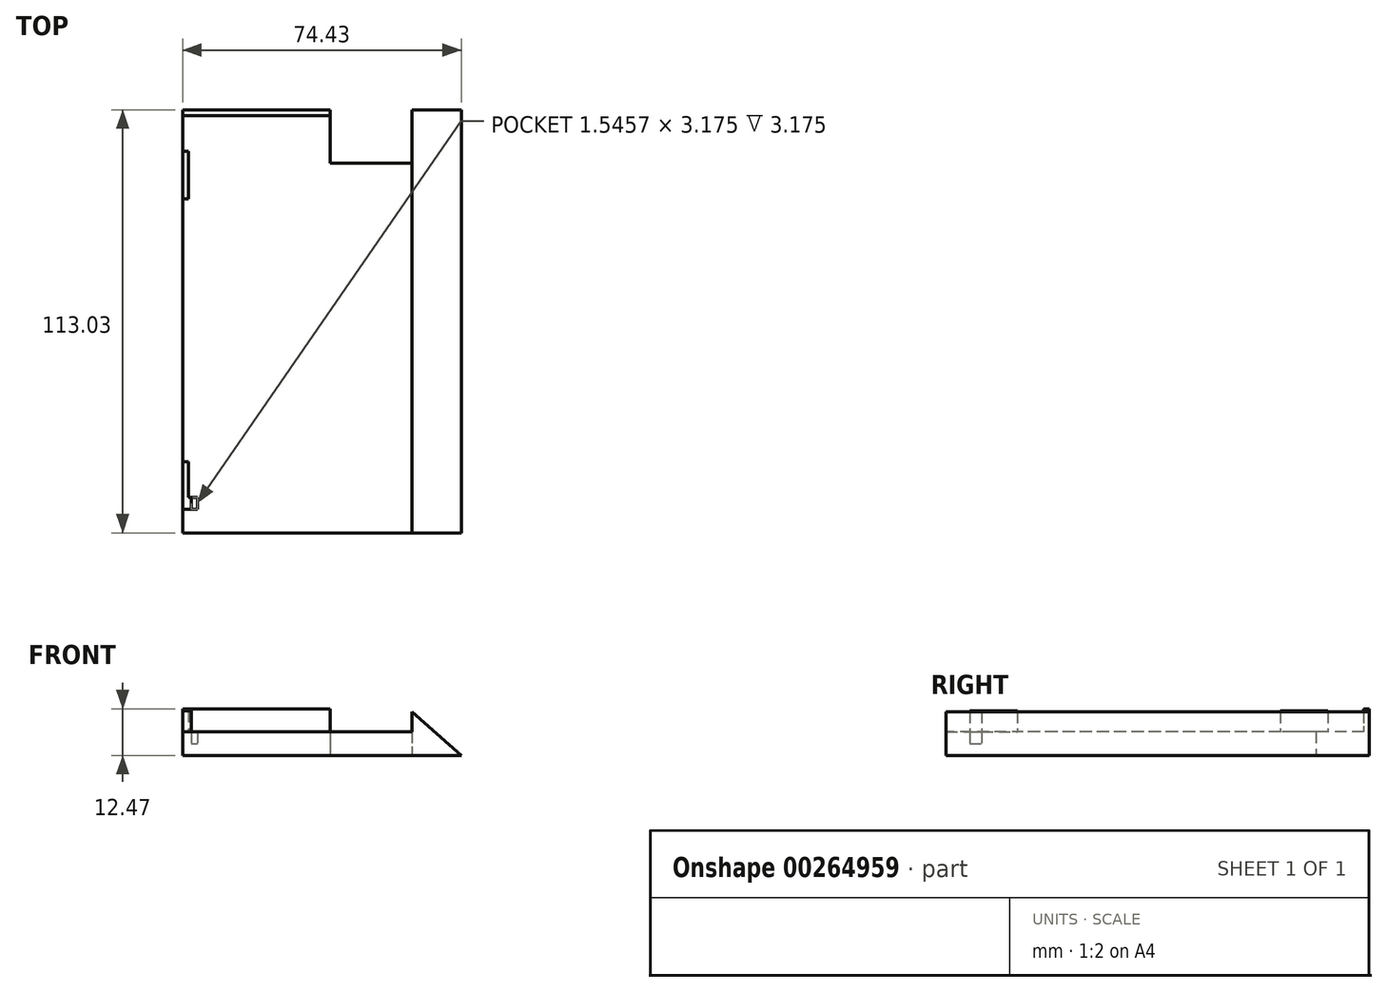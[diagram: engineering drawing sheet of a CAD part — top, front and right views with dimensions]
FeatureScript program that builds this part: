
annotation { "Feature Type Name" : "Feature", "Feature Type Description" : "" }
export const myFeature = defineFeature(function(context is Context, id is Id, definition is map)
    precondition{}
    {
        {
            var Q0;
            Q0=qCreatedBy(makeId("Top.planeOp"),FACE);
            var sketch = newSketch(context, id + "F0", { "sketchPlane" : qUnion([Q0])});
            skLineSegment(sketch, "E0.bottom", {"start": v(-36.5, 51.12) * mm, "end": v(2.98, 51.12) * mm});
            skLineSegment(sketch, "E0.top", {"start": v(-36.5, -61.91) * mm, "end": v(23.83, -61.91) * mm});
            skLineSegment(sketch, "E0.left", {"start": v(-36.5, 51.12) * mm, "end": v(-36.5, -6.67) * mm});
            skPoint(sketch, "E0.middle", {"position": v(0, -10.8) * mm});
            skLineSegment(sketch, "E1", {"start": v(-36.5, -61.91) * mm, "end": v(-34.91, -61.91) * mm});
            skLineSegment(sketch, "E2", {"start": v(-34.91, -61.91) * mm, "end": v(-34.91, -6.67) * mm});
            skLineSegment(sketch, "E3", {"start": v(-36.5, -61.91) * mm, "end": v(1.6, -61.91) * mm});
            skLineSegment(sketch, "E4", {"start": v(36.5, -61.91) * mm, "end": v(24.83, -61.91) * mm});
            skLineSegment(sketch, "E5", {"start": v(24.83, -52.15) * mm, "end": v(24.83, -61.91) * mm});
            skLineSegment(sketch, "E6", {"start": v(24.83, -52.15) * mm, "end": v(24.83, -6.67) * mm});
            skLineSegment(sketch, "E7", {"start": v(-36.5, 51.12) * mm, "end": v(-36.5, 49.53) * mm});
            skLineSegment(sketch, "E8", {"start": v(-36.5, 49.53) * mm, "end": v(2.98, 49.53) * mm});
            skLineSegment(sketch, "E9", {"start": v(2.98, 49.53) * mm, "end": v(2.98, 51.12) * mm});
            skLineSegment(sketch, "E10", {"start": v(2.98, 51.12) * mm, "end": v(2.98, 36.83) * mm});
            skLineSegment(sketch, "E11", {"start": v(2.98, 36.83) * mm, "end": v(24.03, 36.83) * mm});
            skLineSegment(sketch, "E12.trimOffspring", {"start": v(24.83, 51.12) * mm, "end": v(36.5, 51.12) * mm});
            skLineSegment(sketch, "E13", {"start": v(-36.5, -61.91) * mm, "end": v(-36.5, -55.56) * mm});
            skLineSegment(sketch, "E14", {"start": v(-36.5, -55.56) * mm, "end": v(-34.91, -55.56) * mm});
            skLineSegment(sketch, "E15", {"start": v(-36.5, -55.56) * mm, "end": v(-36.5, -52.39) * mm});
            skLineSegment(sketch, "E16", {"start": v(-36.5, -52.39) * mm, "end": v(-34.91, -52.39) * mm});
            skLineSegment(sketch, "E17", {"start": v(-34.91, -52.39) * mm, "end": v(-34.91, -55.56) * mm});
            skLineSegment(sketch, "E18", {"start": v(-36.5, -55.56) * mm, "end": v(-34.09, -55.56) * mm});
            skLineSegment(sketch, "E19", {"start": v(-34.09, -52.39) * mm, "end": v(-34.91, -52.39) * mm});
            skLineSegment(sketch, "E20", {"start": v(-36.5, 51.12) * mm, "end": v(-36.5, 40) * mm});
            skLineSegment(sketch, "E21", {"start": v(-36.5, 40) * mm, "end": v(-34.91, 40) * mm});
            skLineSegment(sketch, "E22", {"start": v(-34.91, 40) * mm, "end": v(-34.91, 36.83) * mm});
            skLineSegment(sketch, "E23", {"start": v(-34.94, 36.83) * mm, "end": v(-36.5, 36.83) * mm});
            skLineSegment(sketch, "E24", {"start": v(-36.5, 36.83) * mm, "end": v(-34.94, 36.83) * mm});
            skLineSegment(sketch, "E25", {"start": v(-33.97, 40) * mm, "end": v(-34.91, 40) * mm});
            skLineSegment(sketch, "E26.bottom", {"start": v(-36.5, -52.39) * mm, "end": v(-35.83, -52.39) * mm});
            skLineSegment(sketch, "E26.top", {"start": v(-35.83, -55.56) * mm, "end": v(-34.09, -55.56) * mm});
            skLineSegment(sketch, "E26.left", {"start": v(-35.83, -52.39) * mm, "end": v(-35.83, -55.56) * mm});
            skLineSegment(sketch, "E27.bottom", {"start": v(-35.72, 36.83) * mm, "end": v(-34.94, 36.83) * mm});
            skLineSegment(sketch, "E27.top", {"start": v(-35.72, 40) * mm, "end": v(-33.97, 40) * mm});
            skLineSegment(sketch, "E27.left", {"start": v(-35.72, 36.83) * mm, "end": v(-35.72, 40) * mm});
            skLineSegment(sketch, "E28.left", {"start": v(-35.83, -54.55) * mm, "end": v(-35.83, -53.37) * mm});
            skLineSegment(sketch, "E29.left", {"start": v(-35.72, 37.85) * mm, "end": v(-35.72, 38.9) * mm});
            skLineSegment(sketch, "E30", {"start": v(-34.09, -55.56) * mm, "end": v(-34.09, -52.39) * mm});
            skPoint(sketch, "E31.orphan", {"position": v(-32.54, -52.39) * mm});
            skPoint(sketch, "E32.start.orphan", {"position": v(-34.94, 36.83) * mm});
            skPoint(sketch, "E33.orphan", {"position": v(-32.54, 40) * mm});
            skPoint(sketch, "E34.orphan", {"position": v(23.83, 51.12) * mm});
            skLineSegment(sketch, "E35.trimOffspring", {"start": v(24.83, -61.91) * mm, "end": v(36.5, -61.91) * mm});
            skPoint(sketch, "E36.end.orphan", {"position": v(28.59, 51.12) * mm});
            skPoint(sketch, "E37.end.orphan", {"position": v(30.17, -61.91) * mm});
            skLineSegment(sketch, "E38", {"start": v(-34.09, -52.39) * mm, "end": v(-32.54, -52.39) * mm});
            skLineSegment(sketch, "E39", {"start": v(-32.54, -55.56) * mm, "end": v(-32.54, -52.39) * mm});
            skLineSegment(sketch, "E40", {"start": v(-32.54, -55.56) * mm, "end": v(-34.09, -55.56) * mm});
            skLineSegment(sketch, "E41", {"start": v(-34.91, 40) * mm, "end": v(-33.97, 40) * mm});
            skLineSegment(sketch, "E42", {"start": v(-34.91, 36.83) * mm, "end": v(-33.97, 36.83) * mm});
            skLineSegment(sketch, "E43", {"start": v(-34.91, 33.66) * mm, "end": v(-36.5, 33.66) * mm});
            skPoint(sketch, "E44.start.orphan", {"position": v(-32.54, 36.83) * mm});
            skLineSegment(sketch, "E45.MirrorCS", {"start": v(-36.5, -49.21) * mm, "end": v(-34.09, -49.21) * mm});
            skLineSegment(sketch, "E46.trimOffspring", {"start": v(-34.91, -52.39) * mm, "end": v(-34.09, -52.39) * mm});
            skLineSegment(sketch, "E47", {"start": v(24.03, 36.83) * mm, "end": v(24.83, 36.83) * mm});
            skLineSegment(sketch, "E48", {"start": v(24.57, 3.5) * mm, "end": v(24.83, 3.5) * mm});
            skLineSegment(sketch, "E49", {"start": v(24.57, -1.27) * mm, "end": v(24.83, -1.27) * mm});
            skLineSegment(sketch, "E50", {"start": v(24.57, -23.81) * mm, "end": v(24.83, -23.81) * mm});
            skLineSegment(sketch, "E51", {"start": v(24.57, -28.57) * mm, "end": v(24.83, -28.57) * mm});
            skLineSegment(sketch, "E52", {"start": v(23.83, -61.91) * mm, "end": v(24.83, -61.91) * mm});
            skPoint(sketch, "E53.end.orphan", {"position": v(39.05, 51.12) * mm});
            skLineSegment(sketch, "E54", {"start": v(-36.5, 33.66) * mm, "end": v(-36.5, 27.3) * mm});
            skLineSegment(sketch, "E55", {"start": v(-36.5, 27.3) * mm, "end": v(-34.91, 27.3) * mm});
            skLineSegment(sketch, "E56", {"start": v(-36.5, -49.21) * mm, "end": v(-36.5, -42.86) * mm});
            skLineSegment(sketch, "E57", {"start": v(-36.5, -42.86) * mm, "end": v(-34.91, -42.86) * mm});
            skLineSegment(sketch, "E58", {"start": v(36.5, -61.91) * mm, "end": v(37.93, -61.91) * mm});
            skLineSegment(sketch, "E59", {"start": v(37.93, -61.91) * mm, "end": v(37.93, -6.67) * mm});
            skLineSegment(sketch, "E60", {"start": v(37.93, 51.12) * mm, "end": v(36.5, 51.12) * mm});
            skLineSegment(sketch, "E61", {"start": v(36.5, -61.91) * mm, "end": v(36.5, -6.67) * mm});
            skLineSegment(sketch, "E62", {"start": v(36.5, 51.12) * mm, "end": v(36.5, -6.67) * mm});
            skLineSegment(sketch, "E63.trimOffspring", {"start": v(-36.5, -6.67) * mm, "end": v(-36.5, -61.91) * mm});
            skLineSegment(sketch, "E64.trimOffspring", {"start": v(-34.91, -6.67) * mm, "end": v(-34.91, 51.12) * mm});
            skLineSegment(sketch, "E65.trimOffspring", {"start": v(24.83, -6.67) * mm, "end": v(24.83, 51.12) * mm});
            skLineSegment(sketch, "E66.trimOffspring", {"start": v(36.5, -6.67) * mm, "end": v(36.5, -61.91) * mm});
            skLineSegment(sketch, "E67.trimOffspring", {"start": v(37.93, -6.67) * mm, "end": v(37.93, 51.12) * mm});
            skLineSegment(sketch, "E68.trimOffspring", {"start": v(36.5, -6.67) * mm, "end": v(36.5, 51.12) * mm});
            skSolve(sketch);
        }
        {
            var Q0;
            {var subQ12=sQuery(id+"F0.wireOp",EDGE,"E0.top");Q0=makeQuery(id+"F0.imprint","IMPRINT",FACE,{"disambiguationData":[TD([[makeQuery(id+"F0.imprint","IMPRINT",EDGE,{"derivedFrom":subQ12}),1.0]])]});}
            var Q1;
            {var subQ0=sQuery(id+"F0.wireOp",EDGE,"E17");Q1=makeQuery(id+"F0.imprint","IMPRINT",FACE,{"disambiguationData":[TD([[makeQuery(id+"F0.imprint","IMPRINT",EDGE,{"derivedFrom":subQ0}),1.0]])]});}
            var Q2;
            {var subQ0=sQuery(id+"F0.wireOp",EDGE,"E22");Q2=makeQuery(id+"F0.imprint","IMPRINT",FACE,{"disambiguationData":[TD([[makeQuery(id+"F0.imprint","IMPRINT",EDGE,{"derivedFrom":subQ0}),1.0]])]});}
            var Q3;
            Q3=makeQuery(id+"F0.imprint","IMPRINT",FACE,{"disambiguationData":[TD([[makeQuery(id+"F0.imprint","IMPRINT",EDGE,{"derivedFrom":sQuery(id+"F0.wireOp",EDGE,"E30")}),-1.0]])]});
            extrude(context, id + "F1", {"entities" : qUnion([Q0, Q1, Q2, Q3]), "depth" : 3.17 * mm, "offsetDistance" : 25.4 * mm});
        }
        {
            var Q0;
            {var subQ0=sQuery(id+"F0.wireOp",EDGE,"E10");var subQ1=sQuery(id+"F0.wireOp",EDGE,"E0.bottom");var subQ2=makeQuery(id+"F0.imprint","INTERSECT",VERTEX,{"derivedFrom":[subQ1,subQ0]});Q0=makeQuery(id+"F0.imprint","IMPRINT",FACE,{"disambiguationData":[TD([[makeQuery(id+"F0.imprint","IMPRINT",EDGE,{"disambiguationData":[TD([[subQ2,1.0]])],"derivedFrom":subQ1}),-1.0]])]});}
            var Q1;
            {var subQ0=sQuery(id+"F0.wireOp",EDGE,"E20");var subQ1=sQuery(id+"F0.wireOp",EDGE,"E0.bottom");var subQ2=makeQuery(id+"F0.imprint","INTERSECT",VERTEX,{"derivedFrom":[subQ1,subQ0]});Q1=makeQuery(id+"F0.imprint","IMPRINT",FACE,{"disambiguationData":[TD([[makeQuery(id+"F0.imprint","IMPRINT",EDGE,{"disambiguationData":[TD([[subQ2,-1.0]])],"derivedFrom":subQ1}),-1.0]])]});}
            extrude(context, id + "F2", {"entities" : qUnion([Q0, Q1]), "operationType" : NewBodyOperationType.ADD, "depth" : 12.47 * mm});
        }
        {
            var Q0;
            Q0=makeQuery(id+"F0.imprint","IMPRINT",FACE,{"disambiguationData":[TD([[makeQuery(id+"F0.imprint","IMPRINT",EDGE,{"derivedFrom":sQuery(id+"F0.wireOp",EDGE,"E30")}),-1.0]])]});
            extrude(context, id + "F3", {"entities" : qUnion([Q0]), "operationType" : NewBodyOperationType.REMOVE, "depth" : 12.7 * mm});
        }
        {
            var Q0;
            Q0=makeQuery(id+"F0.imprint","IMPRINT",FACE,{"disambiguationData":[TD([[makeQuery(id+"F0.imprint","IMPRINT",EDGE,{"derivedFrom":sQuery(id+"F0.wireOp",EDGE,"E30")}),-1.0]])]});
            extrude(context, id + "F4", {"entities" : qUnion([Q0]), "operationType" : NewBodyOperationType.ADD, "depth" : 3.17 * mm});
        }
        {
            var Q0;
            {var subQ2=sQuery(id+"F0.wireOp",EDGE,"E22");Q0=makeQuery(id+"F0.imprint","IMPRINT",FACE,{"disambiguationData":[TD([[makeQuery(id+"F0.imprint","IMPRINT",EDGE,{"derivedFrom":subQ2}),-1.0]])]});}
            var Q1;
            {var subQ0=sQuery(id+"F0.wireOp",EDGE,"E16");Q1=makeQuery(id+"F0.imprint","IMPRINT",FACE,{"disambiguationData":[TD([[makeQuery(id+"F0.imprint","IMPRINT",EDGE,{"derivedFrom":subQ0}),1.0]])]});}
            var Q2;
            {var subQ0=sQuery(id+"F0.wireOp",EDGE,"E15");Q2=makeQuery(id+"F0.imprint","IMPRINT",FACE,{"disambiguationData":[TD([[makeQuery(id+"F0.imprint","IMPRINT",EDGE,{"derivedFrom":subQ0}),-1.0]])]});}
            var Q3;
            {var subQ4=sQuery(id+"F0.wireOp",EDGE,"E16");Q3=makeQuery(id+"F0.imprint","IMPRINT",FACE,{"disambiguationData":[TD([[makeQuery(id+"F0.imprint","IMPRINT",EDGE,{"derivedFrom":subQ4}),-1.0]])]});}
            var Q4;
            {var subQ3=sQuery(id+"F0.wireOp",EDGE,"E21");Q4=makeQuery(id+"F0.imprint","IMPRINT",FACE,{"disambiguationData":[TD([[makeQuery(id+"F0.imprint","IMPRINT",EDGE,{"derivedFrom":subQ3}),-1.0]])]});}
            var Q5;
            {var subQ0=sQuery(id+"F0.wireOp",EDGE,"E43");Q5=makeQuery(id+"F0.imprint","IMPRINT",FACE,{"disambiguationData":[TD([[makeQuery(id+"F0.imprint","IMPRINT",EDGE,{"derivedFrom":subQ0}),1.0]])]});}
            var Q6;
            {var subQ4=sQuery(id+"F0.wireOp",EDGE,"E56");Q6=makeQuery(id+"F0.imprint","IMPRINT",FACE,{"disambiguationData":[TD([[makeQuery(id+"F0.imprint","IMPRINT",EDGE,{"derivedFrom":subQ4}),-1.0]])]});}
            var Q7;
            {var subQ1=sQuery(id+"F0.wireOp",EDGE,"E24");Q7=makeQuery(id+"F0.imprint","IMPRINT",FACE,{"disambiguationData":[TD([[makeQuery(id+"F0.imprint","IMPRINT",EDGE,{"derivedFrom":subQ1}),-1.0]])]});}
            var Q8;
            {var subQ0=sQuery(id+"F0.wireOp",EDGE,"E57");Q8=makeQuery(id+"F0.imprint","IMPRINT",FACE,{"disambiguationData":[TD([[makeQuery(id+"F0.imprint","IMPRINT",EDGE,{"derivedFrom":subQ0}),-1.0]])]});}
            var Q9;
            {var subQ1=sQuery(id+"F0.wireOp",EDGE,"E18");Q9=makeQuery(id+"F0.imprint","IMPRINT",FACE,{"disambiguationData":[TD([[makeQuery(id+"F0.imprint","IMPRINT",EDGE,{"derivedFrom":subQ1}),1.0]])]});}
            extrude(context, id + "F5", {"entities" : qUnion([Q0, Q1, Q2, Q3, Q4, Q5, Q6, Q7, Q8, Q9]), "operationType" : NewBodyOperationType.ADD, "depth" : 11.9 * mm});
        }
        {
            var Q0;
            {var subQ5=sQuery(id+"F0.wireOp",EDGE,"E5");Q0=makeQuery(id+"F0.imprint","IMPRINT",FACE,{"disambiguationData":[TD([[makeQuery(id+"F0.imprint","IMPRINT",EDGE,{"derivedFrom":subQ5}),1.0]])]});}
            var Q1;
            Q1=makeQuery(id+"F0.imprint","IMPRINT",FACE,{"disambiguationData":[TD([[makeQuery(id+"F0.imprint","IMPRINT",EDGE,{"derivedFrom":sQuery(id+"F0.wireOp",EDGE,"E58")}),1.0]])]});
            extrude(context, id + "F6", {"entities" : qUnion([Q0, Q1]), "operationType" : NewBodyOperationType.ADD, "depth" : 11.67 * mm, "offsetDistance" : 25.4 * mm});
        }
        {
            var Q0;
            {var subQ0=sQuery(id+"F0.wireOp",EDGE,"E21");Q0=makeQuery(id+"F0.imprint","IMPRINT",FACE,{"disambiguationData":[TD([[makeQuery(id+"F0.imprint","IMPRINT",EDGE,{"derivedFrom":subQ0}),1.0]])]});}
            var Q1;
            {var subQ0=sQuery(id+"F0.wireOp",EDGE,"E55");Q1=makeQuery(id+"F0.imprint","IMPRINT",FACE,{"disambiguationData":[TD([[makeQuery(id+"F0.imprint","IMPRINT",EDGE,{"derivedFrom":subQ0}),-1.0]])]});}
            var Q2;
            {var subQ1=sQuery(id+"F0.wireOp",EDGE,"E13");Q2=makeQuery(id+"F0.imprint","IMPRINT",FACE,{"disambiguationData":[TD([[makeQuery(id+"F0.imprint","IMPRINT",EDGE,{"derivedFrom":subQ1}),-1.0]])]});}
            var Q3;
            {var subQ0=sQuery(id+"F0.wireOp",EDGE,"E57");Q3=makeQuery(id+"F0.imprint","IMPRINT",FACE,{"disambiguationData":[TD([[makeQuery(id+"F0.imprint","IMPRINT",EDGE,{"derivedFrom":subQ0}),-1.0]])]});}
            var Q4;
            {var subQ0=sQuery(id+"F0.wireOp",EDGE,"E18");Q4=makeQuery(id+"F0.imprint","IMPRINT",FACE,{"disambiguationData":[TD([[makeQuery(id+"F0.imprint","IMPRINT",EDGE,{"derivedFrom":subQ0}),-1.0]])]});}
            extrude(context, id + "F7", {"entities" : qUnion([Q0, Q1, Q2, Q3, Q4]), "operationType" : NewBodyOperationType.ADD, "depth" : 6.35 * mm});
        }
        {
            var Q0;
            Q0=makeQuery(id+"F6.opExtrude","CAP_EDGE",EDGE,{"disambiguationData":[OSD([sQuery(id+"F0.wireOp",EDGE,"E59")])],"isStart":false});
            chamfer(context, id + "F8", {"entities" : qUnion([Q0]), "chamferType" : ChamferType.TWO_OFFSETS, "width1" : 13.1 * mm, "oppositeDirection" : false, "width2" : 11.67 * mm, "tangentPropagation" : true});
        }
    });
